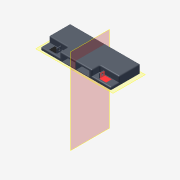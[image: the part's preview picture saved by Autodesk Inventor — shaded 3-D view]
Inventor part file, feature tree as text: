
AUTODESK INVENTOR PART (.ipt)
format: ipt  version: 2013 (Build 170138000, 138)  size: 360,960 bytes
history: native  units: mm (DEFAULTED — no unit token found)
features: sketch x10, extrude x9, fillet x5, plane x5, mirror x3, split x3, hole x1
ambient origin geometry x8: Origin, YZ Plane, XZ Plane, XY Plane, X Axis, Y Axis, Z Axis, Center Point
bodies: Solid1 (feature_tree)
feature tree (36):
  extrude  "Extrusion1"  Depth=74.422mm
  extrude  "Extrusion2"  Depth=21.082mm TaperAngle=0.0deg
  extrude  "Extrusion3"  Depth=21.336mm
  fillet  "Fillet1"  Radius=14.224mm
  fillet  "Fillet3"  Radius=2.54mm
  fillet  "Fillet4"  Radius=2.54mm
  extrude  "Extrusion4"  Depth=0.254mm TaperAngle=0.0deg
  extrude  "Extrusion5"  Depth=12.7mm TaperAngle=0.0deg
  extrude  "Extrusion6"  Depth=12.7mm TaperAngle=0.0deg
  plane  "Work Plane1"
  mirror  "Mirror1"
  mirror  "Mirror2"
  extrude  "Extrusion7"  Depth=20.32mm
  extrude  "Extrusion8"  Depth=19.558mm TaperAngle=0.0deg
  plane  "Work Plane2"
  fillet  "Fillet5"  Radius=33.02mm
  plane  "Work Plane3"
  extrude  "Extrusion9"  Depth=19.05mm TaperAngle=0.0deg
  hole  "Hole1"  [1 undecoded]
  fillet  "Fillet6"  Radius=56.261mm
  mirror  "Mirror3"
  plane  "Work Plane4"
  split  "Split2"
  plane  "Work Plane6"
  split  "Split3"
  split  "Split4"
  sketch  "Sketch1"  dims[d0=179.578mm d1=74.422mm]
  sketch  "Sketch2"  dims[d2=139.7mm d3=0.0mm d4=21.082mm d5=0.0mm]
  sketch  "Sketch3"  dims[d6=49.276mm d7=21.336mm d8=14.224mm d9=0.0mm d10=2.54mm d12=2.54mm]
  sketch  "Sketch4"  dims[d13=2.54mm d14=0.254mm d15=0.0mm]
  sketch  "Sketch5"  dims[d16=1.524mm d17=12.7mm d18=0.0mm]
  sketch  "Sketch6"  dims[d19=5.08mm d20=12.7mm d21=0.0mm]
  sketch  "Sketch7"  dims[d22=20.32mm d23=20.32mm]
  sketch  "Sketch8"  dims[d24=63.5mm d25=19.558mm d26=0.0mm d27=33.02mm]
  sketch  "Sketch9"  dims[d28=3.048mm d29=19.05mm d30=0.0mm]
  sketch  "Sketch10"  dims[d31=181.102mm d32=-127.0mm d34=1.27mm d35=56.261mm d36=11.9888mm d37=11.5062mm d38=2.0066mm d39=0.0mm d40=5.4864mm d41=5.4864mm d42=19.05mm d43=9.525mm d44=6.35mm d45=14.3117mm d46=25.4mm d47=20.594885mm d48=1.27mm d49=14.986mm d50=90.0deg d51=0.0mm]
note: 1 required parameter value undecoded (feature->parameter linkage not recoverable at this tier; creation-order binding heuristic only, values carry confidence <= 0.55)
